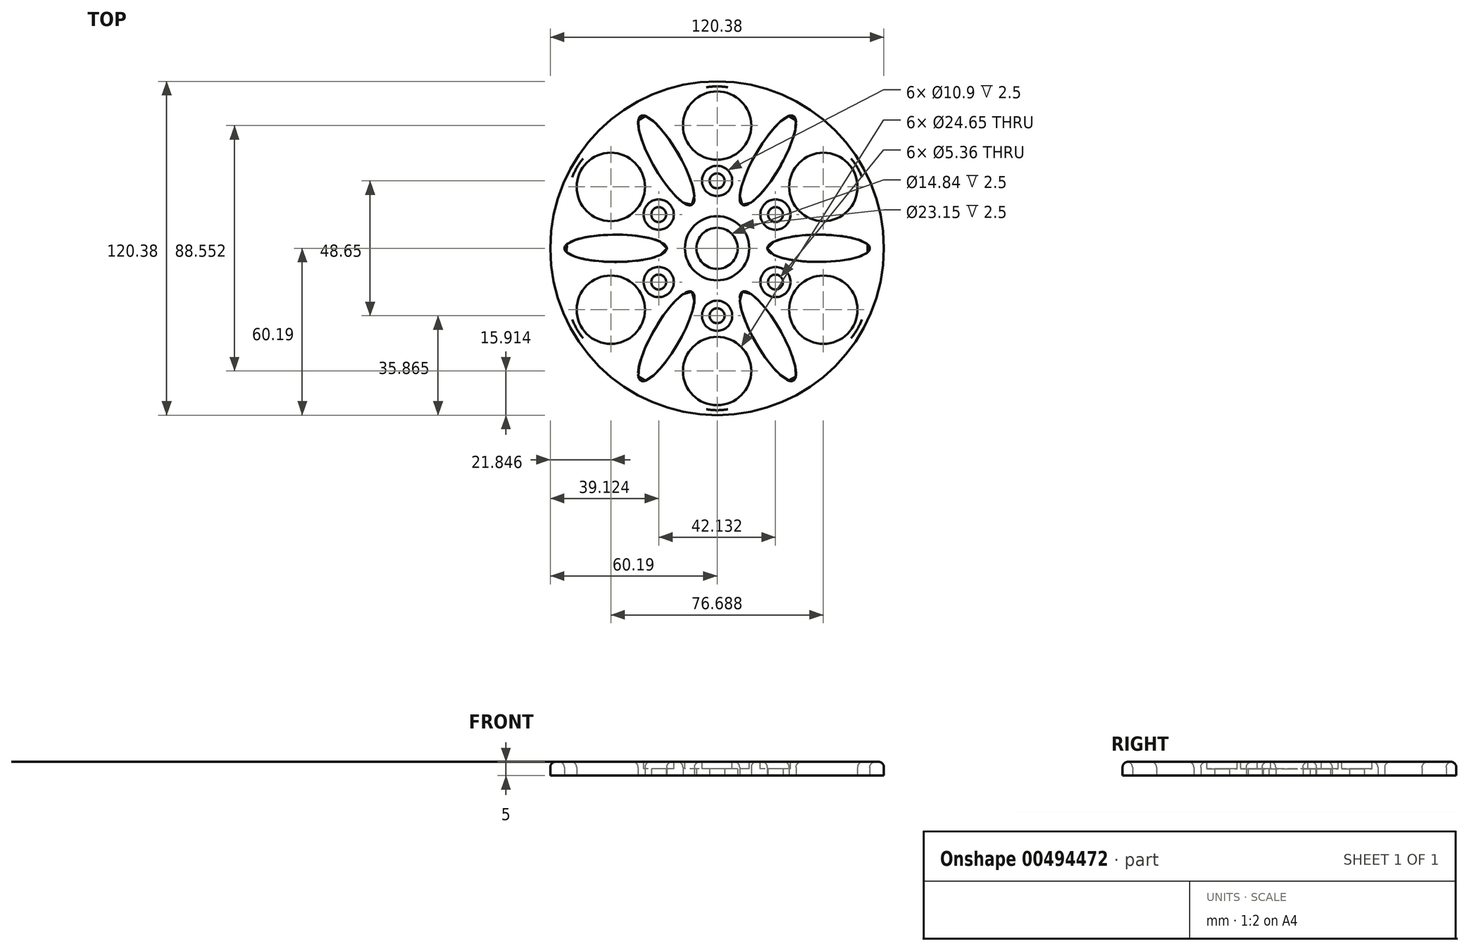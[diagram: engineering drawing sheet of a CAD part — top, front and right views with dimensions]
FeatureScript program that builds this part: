
annotation { "Feature Type Name" : "Feature", "Feature Type Description" : "" }
export const myFeature = defineFeature(function(context is Context, id is Id, definition is map)
    precondition{}
    {
        {
            var Q0;
            Q0=qCreatedBy(makeId("Top.planeOp"),FACE);
            var sketch = newSketch(context, id + "F0", { "sketchPlane" : qUnion([Q0])});
            skCircle(sketch, "E0", {"center": v(0, 0) * mm, "radius": 60.2 * mm});
            skCircle(sketch, "E1", {"center": v(0, 0) * mm, "radius": 7.42 * mm});
            skSolve(sketch);
        }
        {
            var Q0;
            Q0=makeQuery(id+"F0.imprint","IMPRINT",FACE,{"disambiguationData":[TD([[makeQuery(id+"F0.imprint","IMPRINT",EDGE,{"derivedFrom":sQuery(id+"F0.wireOp",EDGE,"E0")}),1.0]])]});
            extrude(context, id + "F1", {"entities" : qUnion([Q0]), "depth" : 5 * mm});
        }
        {
            var Q0;
            Q0=makeQuery(id+"F1.opExtrude","CAP_FACE",FACE,{"disambiguationData":[OSD([sQuery(id+"F0.wireOp",EDGE,"E0"),sQuery(id+"F0.wireOp",EDGE,"E1")])],"isStart":false});
            var sketch = newSketch(context, id + "F2", { "sketchPlane" : qUnion([Q0])});
            skCircle(sketch, "E2", {"center": v(0, 0) * mm, "radius": 11.58 * mm});
            skCircle(sketch, "E3", {"center": v(0, -24.32) * mm, "radius": 2.68 * mm});
            skCircle(sketch, "E4", {"center": v(0, -24.32) * mm, "radius": 5.45 * mm});
            skCircle(sketch, "E5.1.0", {"center": v(21.07, -12.16) * mm, "radius": 5.45 * mm});
            skCircle(sketch, "E5.1.1", {"center": v(21.07, -12.16) * mm, "radius": 2.68 * mm});
            skCircle(sketch, "E5.2.0", {"center": v(21.07, 12.16) * mm, "radius": 5.45 * mm});
            skCircle(sketch, "E5.2.1", {"center": v(21.07, 12.16) * mm, "radius": 2.68 * mm});
            skCircle(sketch, "E5.3.0", {"center": v(0, 24.32) * mm, "radius": 5.45 * mm});
            skCircle(sketch, "E5.3.1", {"center": v(0, 24.32) * mm, "radius": 2.68 * mm});
            skCircle(sketch, "E5.4.0", {"center": v(-21.07, 12.16) * mm, "radius": 5.45 * mm});
            skCircle(sketch, "E5.4.1", {"center": v(-21.07, 12.16) * mm, "radius": 2.68 * mm});
            skCircle(sketch, "E5.5.0", {"center": v(-21.07, -12.16) * mm, "radius": 5.45 * mm});
            skCircle(sketch, "E5.5.1", {"center": v(-21.07, -12.16) * mm, "radius": 2.68 * mm});
            skSolve(sketch);
        }
        {
            var Q0;
            Q0=makeQuery(id+"F2.imprint","IMPRINT",FACE,{"disambiguationData":[TD([[makeQuery(id+"F2.imprint","IMPRINT",EDGE,{"derivedFrom":sQuery(id+"F2.wireOp",EDGE,"E2")}),1.0]])]});
            var Q1;
            Q1=makeQuery(id+"F2.imprint","IMPRINT",FACE,{"disambiguationData":[TD([[makeQuery(id+"F2.imprint","IMPRINT",EDGE,{"derivedFrom":sQuery(id+"F2.wireOp",EDGE,"E5.5.0")}),1.0]])]});
            var Q2;
            Q2=makeQuery(id+"F2.imprint","IMPRINT",FACE,{"disambiguationData":[TD([[makeQuery(id+"F2.imprint","IMPRINT",EDGE,{"derivedFrom":sQuery(id+"F2.wireOp",EDGE,"E5.4.1")}),1.0]])]});
            var Q3;
            Q3=makeQuery(id+"F2.imprint","IMPRINT",FACE,{"disambiguationData":[TD([[makeQuery(id+"F2.imprint","IMPRINT",EDGE,{"derivedFrom":sQuery(id+"F2.wireOp",EDGE,"E5.4.0")}),1.0]])]});
            var Q4;
            Q4=makeQuery(id+"F2.imprint","IMPRINT",FACE,{"disambiguationData":[TD([[makeQuery(id+"F2.imprint","IMPRINT",EDGE,{"derivedFrom":sQuery(id+"F2.wireOp",EDGE,"E3")}),1.0]])]});
            var Q5;
            Q5=makeQuery(id+"F2.imprint","IMPRINT",FACE,{"disambiguationData":[TD([[makeQuery(id+"F2.imprint","IMPRINT",EDGE,{"derivedFrom":sQuery(id+"F2.wireOp",EDGE,"E3")}),-1.0]])]});
            var Q6;
            Q6=makeQuery(id+"F2.imprint","IMPRINT",FACE,{"disambiguationData":[TD([[makeQuery(id+"F2.imprint","IMPRINT",EDGE,{"derivedFrom":sQuery(id+"F2.wireOp",EDGE,"E5.1.1")}),1.0]])]});
            var Q7;
            Q7=makeQuery(id+"F2.imprint","IMPRINT",FACE,{"disambiguationData":[TD([[makeQuery(id+"F2.imprint","IMPRINT",EDGE,{"derivedFrom":sQuery(id+"F2.wireOp",EDGE,"E5.1.0")}),1.0]])]});
            var Q8;
            Q8=makeQuery(id+"F2.imprint","IMPRINT",FACE,{"disambiguationData":[TD([[makeQuery(id+"F2.imprint","IMPRINT",EDGE,{"derivedFrom":sQuery(id+"F2.wireOp",EDGE,"E5.2.1")}),1.0]])]});
            var Q9;
            Q9=makeQuery(id+"F2.imprint","IMPRINT",FACE,{"disambiguationData":[TD([[makeQuery(id+"F2.imprint","IMPRINT",EDGE,{"derivedFrom":sQuery(id+"F2.wireOp",EDGE,"E5.2.0")}),1.0]])]});
            var Q10;
            Q10=makeQuery(id+"F2.imprint","IMPRINT",FACE,{"disambiguationData":[TD([[makeQuery(id+"F2.imprint","IMPRINT",EDGE,{"derivedFrom":sQuery(id+"F2.wireOp",EDGE,"E5.3.1")}),1.0]])]});
            var Q11;
            Q11=makeQuery(id+"F2.imprint","IMPRINT",FACE,{"disambiguationData":[TD([[makeQuery(id+"F2.imprint","IMPRINT",EDGE,{"derivedFrom":sQuery(id+"F2.wireOp",EDGE,"E5.3.0")}),1.0]])]});
            var Q12;
            Q12=makeQuery(id+"F2.imprint","IMPRINT",FACE,{"disambiguationData":[TD([[makeQuery(id+"F2.imprint","IMPRINT",EDGE,{"derivedFrom":sQuery(id+"F2.wireOp",EDGE,"E5.5.1")}),1.0]])]});
            extrude(context, id + "F3", {"entities" : qUnion([Q0, Q1, Q2, Q3, Q4, Q5, Q6, Q7, Q8, Q9, Q10, Q11, Q12]), "operationType" : NewBodyOperationType.REMOVE, "oppositeDirection" : true, "depth" : 2.5 * mm});
        }
        {
            var Q0;
            Q0=qCreatedBy(makeId("Top.planeOp"),FACE);
            var sketch = newSketch(context, id + "F4", { "sketchPlane" : qUnion([Q0])});
            skEllipse(sketch, "E6", {"center": v(-36.61, 0) * mm, "majorRadius": 18.48 * mm, "minorRadius": 4.91 * mm, "majorAxis": v(1, 0)});
            skEllipse(sketch, "E7.1.0", {"center": v(-18.3, -31.7) * mm, "majorRadius": 18.48 * mm, "minorRadius": 4.91 * mm, "majorAxis": v(0.5, 0.87)});
            skEllipse(sketch, "E7.2.0", {"center": v(18.3, -31.7) * mm, "majorRadius": 18.48 * mm, "minorRadius": 4.91 * mm, "majorAxis": v(-0.5, 0.87)});
            skEllipse(sketch, "E7.3.0", {"center": v(36.61, 0) * mm, "majorRadius": 18.48 * mm, "minorRadius": 4.91 * mm, "majorAxis": v(-1, 0)});
            skEllipse(sketch, "E7.4.0", {"center": v(18.3, 31.7) * mm, "majorRadius": 18.48 * mm, "minorRadius": 4.91 * mm, "majorAxis": v(-0.5, -0.87)});
            skEllipse(sketch, "E7.5.0", {"center": v(-18.3, 31.7) * mm, "majorRadius": 18.48 * mm, "minorRadius": 4.91 * mm, "majorAxis": v(0.5, -0.87)});
            skPoint(sketch, "E7.center", {"position": v(0, 0) * mm});
            skCircle(sketch, "E8", {"center": v(0, 44.28) * mm, "radius": 12.32 * mm});
            skCircle(sketch, "E9.1.0", {"center": v(-38.34, 22.14) * mm, "radius": 12.32 * mm});
            skCircle(sketch, "E9.2.0", {"center": v(-38.34, -22.14) * mm, "radius": 12.32 * mm});
            skCircle(sketch, "E9.3.0", {"center": v(0, -44.28) * mm, "radius": 12.32 * mm});
            skCircle(sketch, "E9.4.0", {"center": v(38.34, -22.14) * mm, "radius": 12.32 * mm});
            skCircle(sketch, "E9.5.0", {"center": v(38.34, 22.14) * mm, "radius": 12.32 * mm});
            skSolve(sketch);
        }
        {
            var Q0;
            Q0 = qSketchRegion(id + "F4", true);
            extrude(context, id + "F5", {"entities" : qUnion([Q0]), "operationType" : NewBodyOperationType.REMOVE, "endBound" : BoundingType.THROUGH_ALL, "depth" : 25 * mm, "offsetDistance" : 25 * mm});
        }
        {
            var Q0;
            Q0=makeQuery(id+"F1.opExtrude","CAP_EDGE",EDGE,{"disambiguationData":[OSD([sQuery(id+"F0.wireOp",EDGE,"E0")])],"isStart":false});
            var Q1;
            Q1=makeQuery(id+"F5.boolean.opBoolean","INTERSECT",EDGE,{"derivedFrom":[makeQuery(id+"F1.opExtrude","CAP_FACE",FACE,{"disambiguationData":[OSD([sQuery(id+"F0.wireOp",EDGE,"E0"),sQuery(id+"F0.wireOp",EDGE,"E1")])],"isStart":false}),makeQuery(id+"F5.opExtrude","SWEPT_FACE",FACE,{"disambiguationData":[OSD([sQuery(id+"F4.wireOp",EDGE,"E7.2.0")])]})]});
            var Q2;
            Q2=makeQuery(id+"F5.boolean.opBoolean","INTERSECT",EDGE,{"derivedFrom":[makeQuery(id+"F1.opExtrude","CAP_FACE",FACE,{"disambiguationData":[OSD([sQuery(id+"F0.wireOp",EDGE,"E0"),sQuery(id+"F0.wireOp",EDGE,"E1")])],"isStart":false}),makeQuery(id+"F5.opExtrude","SWEPT_FACE",FACE,{"disambiguationData":[OSD([sQuery(id+"F4.wireOp",EDGE,"E7.3.0")])]})]});
            var Q3;
            Q3=makeQuery(id+"F5.boolean.opBoolean","INTERSECT",EDGE,{"derivedFrom":[makeQuery(id+"F1.opExtrude","CAP_FACE",FACE,{"disambiguationData":[OSD([sQuery(id+"F0.wireOp",EDGE,"E0"),sQuery(id+"F0.wireOp",EDGE,"E1")])],"isStart":false}),makeQuery(id+"F5.opExtrude","SWEPT_FACE",FACE,{"disambiguationData":[OSD([sQuery(id+"F4.wireOp",EDGE,"E7.4.0")])]})]});
            var Q4;
            Q4=makeQuery(id+"F5.boolean.opBoolean","INTERSECT",EDGE,{"derivedFrom":[makeQuery(id+"F1.opExtrude","CAP_FACE",FACE,{"disambiguationData":[OSD([sQuery(id+"F0.wireOp",EDGE,"E0"),sQuery(id+"F0.wireOp",EDGE,"E1")])],"isStart":false}),makeQuery(id+"F5.opExtrude","SWEPT_FACE",FACE,{"disambiguationData":[OSD([sQuery(id+"F4.wireOp",EDGE,"E7.5.0")])]})]});
            var Q5;
            Q5=makeQuery(id+"F5.boolean.opBoolean","INTERSECT",EDGE,{"derivedFrom":[makeQuery(id+"F1.opExtrude","CAP_FACE",FACE,{"disambiguationData":[OSD([sQuery(id+"F0.wireOp",EDGE,"E0"),sQuery(id+"F0.wireOp",EDGE,"E1")])],"isStart":false}),makeQuery(id+"F5.opExtrude","SWEPT_FACE",FACE,{"disambiguationData":[OSD([sQuery(id+"F4.wireOp",EDGE,"E6")])]})]});
            var Q6;
            Q6=makeQuery(id+"F5.boolean.opBoolean","INTERSECT",EDGE,{"derivedFrom":[makeQuery(id+"F1.opExtrude","CAP_FACE",FACE,{"disambiguationData":[OSD([sQuery(id+"F0.wireOp",EDGE,"E0"),sQuery(id+"F0.wireOp",EDGE,"E1")])],"isStart":false}),makeQuery(id+"F5.opExtrude","SWEPT_FACE",FACE,{"disambiguationData":[OSD([sQuery(id+"F4.wireOp",EDGE,"E7.1.0")])]})]});
            var Q7;
            Q7=makeQuery(id+"F5.boolean.opBoolean","INTERSECT",EDGE,{"derivedFrom":[makeQuery(id+"F1.opExtrude","CAP_FACE",FACE,{"disambiguationData":[OSD([sQuery(id+"F0.wireOp",EDGE,"E0"),sQuery(id+"F0.wireOp",EDGE,"E1")])],"isStart":false}),makeQuery(id+"F5.opExtrude","SWEPT_FACE",FACE,{"disambiguationData":[OSD([sQuery(id+"F4.wireOp",EDGE,"E8")])]})]});
            var Q8;
            Q8=makeQuery(id+"F5.boolean.opBoolean","INTERSECT",EDGE,{"derivedFrom":[makeQuery(id+"F1.opExtrude","CAP_FACE",FACE,{"disambiguationData":[OSD([sQuery(id+"F0.wireOp",EDGE,"E0"),sQuery(id+"F0.wireOp",EDGE,"E1")])],"isStart":false}),makeQuery(id+"F5.opExtrude","SWEPT_FACE",FACE,{"disambiguationData":[OSD([sQuery(id+"F4.wireOp",EDGE,"E9.5.0")])]})]});
            var Q9;
            Q9=makeQuery(id+"F5.boolean.opBoolean","INTERSECT",EDGE,{"derivedFrom":[makeQuery(id+"F1.opExtrude","CAP_FACE",FACE,{"disambiguationData":[OSD([sQuery(id+"F0.wireOp",EDGE,"E0"),sQuery(id+"F0.wireOp",EDGE,"E1")])],"isStart":false}),makeQuery(id+"F5.opExtrude","SWEPT_FACE",FACE,{"disambiguationData":[OSD([sQuery(id+"F4.wireOp",EDGE,"E9.4.0")])]})]});
            var Q10;
            Q10=makeQuery(id+"F5.boolean.opBoolean","INTERSECT",EDGE,{"derivedFrom":[makeQuery(id+"F1.opExtrude","CAP_FACE",FACE,{"disambiguationData":[OSD([sQuery(id+"F0.wireOp",EDGE,"E0"),sQuery(id+"F0.wireOp",EDGE,"E1")])],"isStart":false}),makeQuery(id+"F5.opExtrude","SWEPT_FACE",FACE,{"disambiguationData":[OSD([sQuery(id+"F4.wireOp",EDGE,"E9.3.0")])]})]});
            var Q11;
            Q11=makeQuery(id+"F5.boolean.opBoolean","INTERSECT",EDGE,{"derivedFrom":[makeQuery(id+"F1.opExtrude","CAP_FACE",FACE,{"disambiguationData":[OSD([sQuery(id+"F0.wireOp",EDGE,"E0"),sQuery(id+"F0.wireOp",EDGE,"E1")])],"isStart":false}),makeQuery(id+"F5.opExtrude","SWEPT_FACE",FACE,{"disambiguationData":[OSD([sQuery(id+"F4.wireOp",EDGE,"E9.2.0")])]})]});
            var Q12;
            Q12=makeQuery(id+"F5.boolean.opBoolean","INTERSECT",EDGE,{"derivedFrom":[makeQuery(id+"F1.opExtrude","CAP_FACE",FACE,{"disambiguationData":[OSD([sQuery(id+"F0.wireOp",EDGE,"E0"),sQuery(id+"F0.wireOp",EDGE,"E1")])],"isStart":false}),makeQuery(id+"F5.opExtrude","SWEPT_FACE",FACE,{"disambiguationData":[OSD([sQuery(id+"F4.wireOp",EDGE,"E9.1.0")])]})]});
            fillet(context, id + "F6", {"entities" : qUnion([Q0, Q1, Q2, Q3, Q4, Q5, Q6, Q7, Q8, Q9, Q10, Q11, Q12]), "radius" : 2 * mm, "tangentPropagation" : true, "allowEdgeOverflow" : false});
        }
        {
            var Q0;
            Q0=qCreatedBy(makeId("Top.planeOp"),FACE);
            var sketch = newSketch(context, id + "F7", { "sketchPlane" : qUnion([Q0])});
            skCircle(sketch, "E10", {"center": v(0, 0) * mm, "radius": 11.58 * mm});
            skCircle(sketch, "E11", {"center": v(0, -24.32) * mm, "radius": 2.68 * mm});
            skCircle(sketch, "E12", {"center": v(0, -24.32) * mm, "radius": 5.45 * mm});
            skCircle(sketch, "E13.1.0", {"center": v(21.07, -12.16) * mm, "radius": 5.45 * mm});
            skCircle(sketch, "E13.1.1", {"center": v(21.07, -12.16) * mm, "radius": 2.68 * mm});
            skCircle(sketch, "E13.2.0", {"center": v(21.07, 12.16) * mm, "radius": 5.45 * mm});
            skCircle(sketch, "E13.2.1", {"center": v(21.07, 12.16) * mm, "radius": 2.68 * mm});
            skCircle(sketch, "E13.3.0", {"center": v(0, 24.32) * mm, "radius": 5.45 * mm});
            skCircle(sketch, "E13.3.1", {"center": v(0, 24.32) * mm, "radius": 2.68 * mm});
            skCircle(sketch, "E13.4.0", {"center": v(-21.07, 12.16) * mm, "radius": 5.45 * mm});
            skCircle(sketch, "E13.4.1", {"center": v(-21.07, 12.16) * mm, "radius": 2.68 * mm});
            skCircle(sketch, "E13.5.0", {"center": v(-21.07, -12.16) * mm, "radius": 5.45 * mm});
            skCircle(sketch, "E13.5.1", {"center": v(-21.07, -12.16) * mm, "radius": 2.68 * mm});
            skSolve(sketch);
        }
        {
            var Q0;
            Q0=makeQuery(id+"F7.imprint","IMPRINT",FACE,{"disambiguationData":[TD([[makeQuery(id+"F7.imprint","IMPRINT",EDGE,{"derivedFrom":sQuery(id+"F7.wireOp",EDGE,"E11")}),1.0]])]});
            var Q1;
            Q1=makeQuery(id+"F7.imprint","IMPRINT",FACE,{"disambiguationData":[TD([[makeQuery(id+"F7.imprint","IMPRINT",EDGE,{"derivedFrom":sQuery(id+"F7.wireOp",EDGE,"E13.5.1")}),1.0]])]});
            var Q2;
            Q2=makeQuery(id+"F7.imprint","IMPRINT",FACE,{"disambiguationData":[TD([[makeQuery(id+"F7.imprint","IMPRINT",EDGE,{"derivedFrom":sQuery(id+"F7.wireOp",EDGE,"E13.4.1")}),1.0]])]});
            var Q3;
            Q3=makeQuery(id+"F7.imprint","IMPRINT",FACE,{"disambiguationData":[TD([[makeQuery(id+"F7.imprint","IMPRINT",EDGE,{"derivedFrom":sQuery(id+"F7.wireOp",EDGE,"E13.3.1")}),1.0]])]});
            var Q4;
            Q4=makeQuery(id+"F7.imprint","IMPRINT",FACE,{"disambiguationData":[TD([[makeQuery(id+"F7.imprint","IMPRINT",EDGE,{"derivedFrom":sQuery(id+"F7.wireOp",EDGE,"E13.2.1")}),1.0]])]});
            var Q5;
            Q5=makeQuery(id+"F7.imprint","IMPRINT",FACE,{"disambiguationData":[TD([[makeQuery(id+"F7.imprint","IMPRINT",EDGE,{"derivedFrom":sQuery(id+"F7.wireOp",EDGE,"E13.1.1")}),1.0]])]});
            var Q6;
            Q6=sQuery(id+"F7.wireOp",EDGE,"E13.2.1");
            var Q7;
            Q7=sQuery(id+"F7.wireOp",EDGE,"E13.1.1");
            var Q8;
            Q8=sQuery(id+"F7.wireOp",EDGE,"E11");
            var Q9;
            Q9=sQuery(id+"F7.wireOp",EDGE,"E13.5.1");
            var Q10;
            Q10=sQuery(id+"F7.wireOp",EDGE,"E13.4.1");
            var Q11;
            Q11=sQuery(id+"F7.wireOp",EDGE,"E13.3.1");
            extrude(context, id + "F8", {"entities" : qUnion([Q0, Q1, Q2, Q3, Q4, Q5]), "operationType" : NewBodyOperationType.REMOVE, "surfaceEntities" : qUnion([Q6, Q7, Q8, Q9, Q10, Q11]), "depth" : 25 * mm, "offsetDistance" : 25 * mm});
        }
    });
